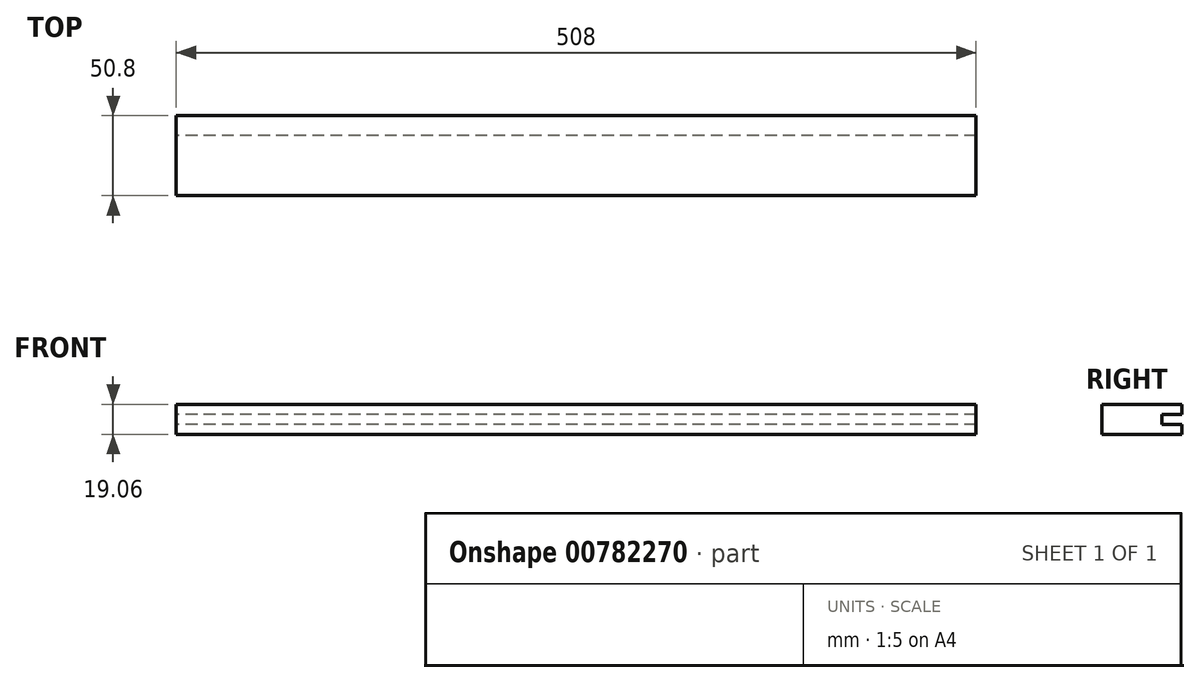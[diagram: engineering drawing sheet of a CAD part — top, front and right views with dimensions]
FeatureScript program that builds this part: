
annotation { "Feature Type Name" : "Feature", "Feature Type Description" : "" }
export const myFeature = defineFeature(function(context is Context, id is Id, definition is map)
    precondition{}
    {
        {
            var Q0;
            Q0=qCreatedBy(makeId("Front.planeOp"),FACE);
            var sketch = newSketch(context, id + "F0", { "sketchPlane" : qUnion([Q0])});
            skLineSegment(sketch, "E0.bottom", {"start": v(-254, 9.52) * mm, "end": v(254, 9.52) * mm});
            skLineSegment(sketch, "E0.top", {"start": v(-254, -9.52) * mm, "end": v(254, -9.52) * mm});
            skLineSegment(sketch, "E0.left", {"start": v(-254, 9.52) * mm, "end": v(-254, -9.52) * mm});
            skLineSegment(sketch, "E0.right", {"start": v(254, 9.52) * mm, "end": v(254, -9.52) * mm});
            skLineSegment(sketch, "E1", {"start": v(-254, 0) * mm, "end": v(254, 0) * mm, "construction": true});
            skSolve(sketch);
        }
        {
            var Q0;
            Q0 = qSketchRegion(id + "F0", true);
            extrude(context, id + "F1", {"entities" : qUnion([Q0]), "depth" : 50.8 * mm, "offsetDistance" : 25.4 * mm});
        }
        {
            var Q0;
            Q0=makeQuery(id+"F1.opExtrude","CAP_FACE",FACE,{"disambiguationData":[OSD([sQuery(id+"F0.wireOp",EDGE,"E0.bottom"),sQuery(id+"F0.wireOp",EDGE,"E0.top"),sQuery(id+"F0.wireOp",EDGE,"E0.left"),sQuery(id+"F0.wireOp",EDGE,"E0.right")])],"isStart":true});
            var sketch = newSketch(context, id + "F2", { "sketchPlane" : qUnion([Q0])});
            skLineSegment(sketch, "E2.bottom", {"start": v(-254, 3.17) * mm, "end": v(254, 3.17) * mm});
            skLineSegment(sketch, "E2.top", {"start": v(-254, -3.18) * mm, "end": v(254, -3.18) * mm});
            skLineSegment(sketch, "E2.left", {"start": v(-254, 3.17) * mm, "end": v(-254, -3.18) * mm});
            skLineSegment(sketch, "E2.right", {"start": v(254, 3.17) * mm, "end": v(254, -3.18) * mm});
            skLineSegment(sketch, "E3", {"start": v(254, 3.17) * mm, "end": v(-254, -3.17) * mm, "construction": true});
            skSolve(sketch);
        }
        {
            var Q0;
            Q0 = qSketchRegion(id + "F2", true);
            extrude(context, id + "F3", {"entities" : qUnion([Q0]), "operationType" : NewBodyOperationType.REMOVE, "oppositeDirection" : true, "depth" : 12.7 * mm, "offsetDistance" : 25.4 * mm});
        }
    });
